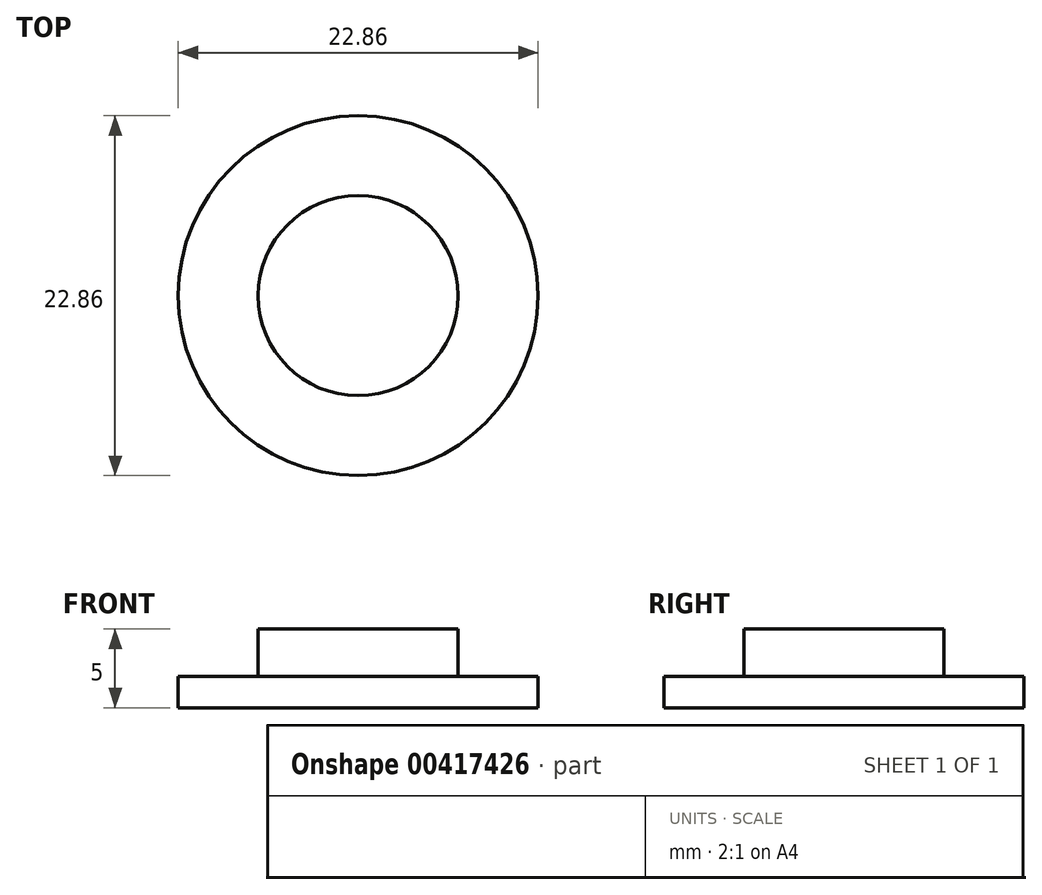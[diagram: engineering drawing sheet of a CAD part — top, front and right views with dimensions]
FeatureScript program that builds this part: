
annotation { "Feature Type Name" : "Feature", "Feature Type Description" : "" }
export const myFeature = defineFeature(function(context is Context, id is Id, definition is map)
    precondition{}
    {
        {
            assignVariable(context, id + "F0", {"name" : "outerShaftHeight", "anyValue" : 2});
        }
        {
            assignVariable(context, id + "F1", {"name" : "innerShaftHeight", "anyValue" : 3});
        }
        {
            var Q0;
            Q0=qCreatedBy(makeId("Top.planeOp"),FACE);
            var sketch = newSketch(context, id + "F2", { "sketchPlane" : qUnion([Q0])});
            skCircle(sketch, "E0", {"center": v(0, 0) * mm, "radius": 11.43 * mm});
            skCircle(sketch, "E1", {"center": v(0, 0) * mm, "radius": 6.35 * mm});
            skSolve(sketch);
        }
        {
            var Q0;
            Q0=makeQuery(id+"F2.imprint","IMPRINT",FACE,{"disambiguationData":[TD([[makeQuery(id+"F2.imprint","IMPRINT",EDGE,{"derivedFrom":sQuery(id+"F2.wireOp",EDGE,"E0")}),1.0]])]});
            extrude(context, id + "F3", {"entities" : qUnion([Q0]), "depth" : (getVariable(context, 'outerShaftHeight')) * mm, "offsetDistance" : 25.4 * mm});
        }
        {
            var Q0;
            Q0=makeQuery(id+"F2.imprint","IMPRINT",FACE,{"disambiguationData":[TD([[makeQuery(id+"F2.imprint","IMPRINT",EDGE,{"derivedFrom":sQuery(id+"F2.wireOp",EDGE,"E1")}),1.0]])]});
            extrude(context, id + "F4", {"entities" : qUnion([Q0]), "operationType" : NewBodyOperationType.ADD, "depth" : (getVariable(context, 'outerShaftHeight') + getVariable(context, 'innerShaftHeight')) * mm, "offsetDistance" : 25.4 * mm});
        }
    });
